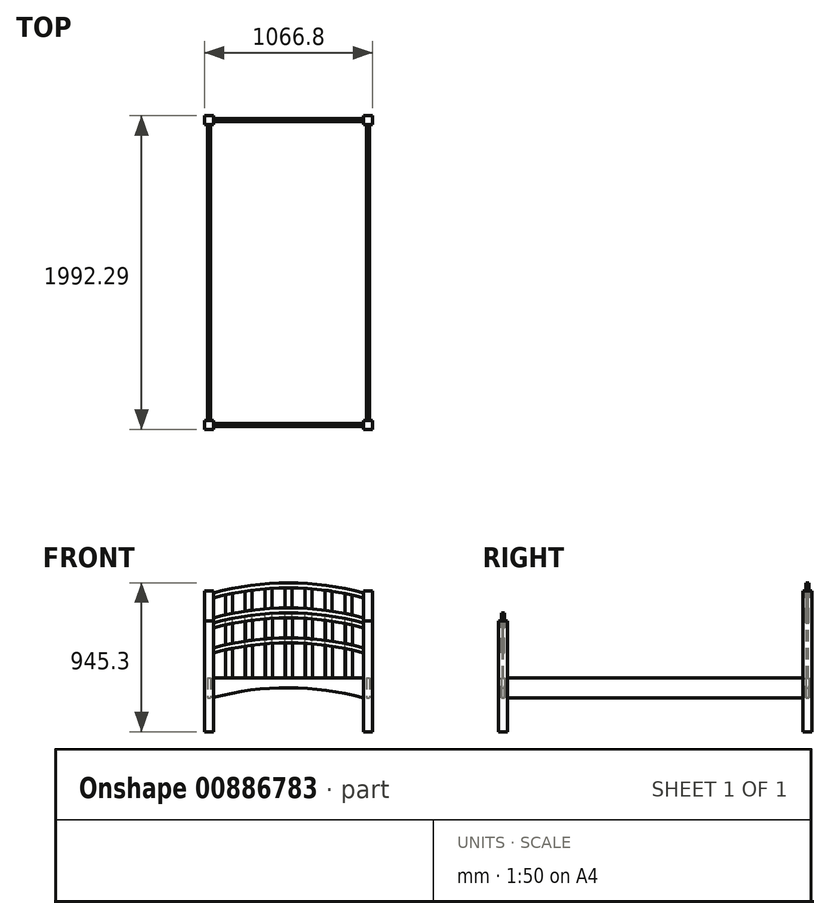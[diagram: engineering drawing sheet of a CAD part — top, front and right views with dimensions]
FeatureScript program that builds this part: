
annotation { "Feature Type Name" : "Feature", "Feature Type Description" : "" }
export const myFeature = defineFeature(function(context is Context, id is Id, definition is map)
    precondition{}
    {
        {
            var Q0;
            Q0=qCreatedBy(makeId("Front.planeOp"),FACE);
            var sketch = newSketch(context, id + "F0", { "sketchPlane" : qUnion([Q0])});
            skLineSegment(sketch, "E0.bottom", {"start": v(-533.4, 352.42) * mm, "end": v(-476.25, 352.42) * mm});
            skLineSegment(sketch, "E0.top", {"start": v(-533.4, -352.43) * mm, "end": v(-476.25, -352.43) * mm});
            skLineSegment(sketch, "E0.left", {"start": v(-533.4, 352.42) * mm, "end": v(-533.4, -352.43) * mm});
            skLineSegment(sketch, "E0.right", {"start": v(533.4, 352.43) * mm, "end": v(533.4, -352.42) * mm});
            skPoint(sketch, "E0.middle", {"position": v(0, 0) * mm});
            skLineSegment(sketch, "E1", {"start": v(-476.25, -352.43) * mm, "end": v(-476.25, 352.42) * mm});
            skLineSegment(sketch, "E2", {"start": v(476.25, 352.43) * mm, "end": v(476.25, -352.43) * mm});
            skPoint(sketch, "E3", {"position": v(0, -73.03) * mm});
            skLineSegment(sketch, "E4.trimOffspring", {"start": v(476.25, -352.43) * mm, "end": v(533.4, -352.42) * mm});
            skLineSegment(sketch, "E5.bottom", {"start": v(-476.25, -9.53) * mm, "end": v(476.25, -9.52) * mm});
            skArc(sketch, "E6", {"start": v(476.25, -136.53) * mm, "mid": v(0.11, -73.03) * mm, "end": v(-476.25, -134.82) * mm});
            skPoint(sketch, "E7", {"position": v(-476.25, 149.22) * mm});
            skPoint(sketch, "E8", {"position": v(-476.25, 180.97) * mm});
            skPoint(sketch, "E9", {"position": v(476.25, 180.97) * mm});
            skPoint(sketch, "E10", {"position": v(476.25, 149.22) * mm});
            skPoint(sketch, "E11", {"position": v(-476.25, 307.97) * mm});
            skPoint(sketch, "E12", {"position": v(-476.25, 339.72) * mm});
            skPoint(sketch, "E13", {"position": v(476.25, 339.73) * mm});
            skPoint(sketch, "E14", {"position": v(476.25, 307.98) * mm});
            skArc(sketch, "E15", {"start": v(476.25, 339.73) * mm, "mid": v(0, 402.37) * mm, "end": v(-476.25, 339.73) * mm});
            skArc(sketch, "E16", {"start": v(476.25, 307.97) * mm, "mid": v(0, 370.62) * mm, "end": v(-476.25, 307.97) * mm});
            skLineSegment(sketch, "E17.trimOffspring", {"start": v(476.25, 352.43) * mm, "end": v(533.4, 352.43) * mm});
            skArc(sketch, "E18", {"start": v(476.25, 180.98) * mm, "mid": v(0, 243.62) * mm, "end": v(-476.25, 180.98) * mm});
            skArc(sketch, "E19", {"start": v(476.25, 149.22) * mm, "mid": v(0, 211.87) * mm, "end": v(-476.25, 149.22) * mm});
            skLineSegment(sketch, "E20.bottom", {"start": v(-400.05, -9.53) * mm, "end": v(-355.6, -9.53) * mm});
            skLineSegment(sketch, "E20.left", {"start": v(-400.05, -9.53) * mm, "end": v(-400.05, 167.9) * mm});
            skLineSegment(sketch, "E20.right", {"start": v(-355.6, -9.53) * mm, "end": v(-355.6, 177.21) * mm});
            skLineSegment(sketch, "E21.1.0.0", {"start": v(-228.6, -9.53) * mm, "end": v(-228.6, 197.63) * mm});
            skLineSegment(sketch, "E21.1.0.1", {"start": v(-273.05, -9.53) * mm, "end": v(-273.05, 191.52) * mm});
            skLineSegment(sketch, "E21.1.0.2", {"start": v(-273.05, -9.53) * mm, "end": v(-228.6, -9.53) * mm});
            skLineSegment(sketch, "E21.2.0.0", {"start": v(-101.6, -9.53) * mm, "end": v(-101.6, 209.07) * mm});
            skLineSegment(sketch, "E21.2.0.1", {"start": v(-146.05, -9.53) * mm, "end": v(-146.05, 206.07) * mm});
            skLineSegment(sketch, "E21.2.0.2", {"start": v(-146.05, -9.53) * mm, "end": v(-101.6, -9.53) * mm});
            skLineSegment(sketch, "E21.3.0.0", {"start": v(25.4, -9.53) * mm, "end": v(25.4, 211.7) * mm});
            skLineSegment(sketch, "E21.3.0.1", {"start": v(-19.05, -9.53) * mm, "end": v(-19.05, 211.77) * mm});
            skLineSegment(sketch, "E21.3.0.2", {"start": v(-19.05, -9.53) * mm, "end": v(25.4, -9.53) * mm});
            skLineSegment(sketch, "E21.4.0.0", {"start": v(152.4, -9.53) * mm, "end": v(152.4, 205.56) * mm});
            skLineSegment(sketch, "E21.4.0.1", {"start": v(107.95, -9.53) * mm, "end": v(107.95, 208.7) * mm});
            skLineSegment(sketch, "E21.4.0.2", {"start": v(107.95, -9.53) * mm, "end": v(152.4, -9.53) * mm});
            skLineSegment(sketch, "E21.5.0.0", {"start": v(279.4, -9.53) * mm, "end": v(279.4, 190.55) * mm});
            skLineSegment(sketch, "E21.5.0.1", {"start": v(234.95, -9.53) * mm, "end": v(234.95, 196.82) * mm});
            skLineSegment(sketch, "E21.5.0.2", {"start": v(234.95, -9.53) * mm, "end": v(279.4, -9.53) * mm});
            skLineSegment(sketch, "E21.6.0.0", {"start": v(406.4, -9.53) * mm, "end": v(406.4, 166.47) * mm});
            skLineSegment(sketch, "E21.6.0.1", {"start": v(361.95, -9.53) * mm, "end": v(361.95, 175.95) * mm});
            skLineSegment(sketch, "E21.6.0.2", {"start": v(361.95, -9.53) * mm, "end": v(406.4, -9.53) * mm});
            skLineSegment(sketch, "E21.direction1", {"start": v(-355.6, -9.53) * mm, "end": v(-228.6, -9.53) * mm, "construction": true});
            skPoint(sketch, "E22.orphan", {"position": v(-400.05, 377.28) * mm});
            skPoint(sketch, "E23.orphan", {"position": v(-355.6, 377.28) * mm});
            skLineSegment(sketch, "E24.trimOffspring", {"start": v(-355.6, 208.96) * mm, "end": v(-355.6, 335.96) * mm});
            skLineSegment(sketch, "E25.trimOffspring", {"start": v(-400.05, 199.65) * mm, "end": v(-400.05, 326.65) * mm});
            skLineSegment(sketch, "E26.trimOffspring", {"start": v(-273.05, 223.27) * mm, "end": v(-273.05, 350.27) * mm});
            skLineSegment(sketch, "E27.trimOffspring", {"start": v(-228.6, 229.38) * mm, "end": v(-228.6, 356.38) * mm});
            skLineSegment(sketch, "E28.trimOffspring", {"start": v(-146.05, 237.82) * mm, "end": v(-146.05, 364.82) * mm});
            skLineSegment(sketch, "E29.trimOffspring", {"start": v(-101.6, 240.82) * mm, "end": v(-101.6, 367.82) * mm});
            skLineSegment(sketch, "E30.trimOffspring", {"start": v(-19.05, 243.52) * mm, "end": v(-19.05, 370.52) * mm});
            skLineSegment(sketch, "E31.trimOffspring", {"start": v(25.4, 243.45) * mm, "end": v(25.4, 370.45) * mm});
            skLineSegment(sketch, "E32.trimOffspring", {"start": v(107.95, 240.46) * mm, "end": v(107.95, 367.46) * mm});
            skLineSegment(sketch, "E33.trimOffspring", {"start": v(152.4, 237.3) * mm, "end": v(152.4, 364.3) * mm});
            skLineSegment(sketch, "E34.trimOffspring", {"start": v(234.95, 228.57) * mm, "end": v(234.95, 355.57) * mm});
            skLineSegment(sketch, "E35.trimOffspring", {"start": v(279.4, 222.3) * mm, "end": v(279.4, 349.3) * mm});
            skLineSegment(sketch, "E36.trimOffspring", {"start": v(361.95, 207.7) * mm, "end": v(361.95, 334.7) * mm});
            skLineSegment(sketch, "E37.trimOffspring", {"start": v(406.4, 198.22) * mm, "end": v(406.4, 325.22) * mm});
            skPoint(sketch, "E38.orphan", {"position": v(279.4, 377.28) * mm});
            skPoint(sketch, "E39.orphan", {"position": v(107.95, 377.28) * mm});
            skPoint(sketch, "E40.orphan", {"position": v(-19.05, 377.28) * mm});
            skPoint(sketch, "E41.orphan", {"position": v(-101.6, 377.28) * mm});
            skPoint(sketch, "E42.orphan", {"position": v(-228.6, 377.28) * mm});
            skSolve(sketch);
        }
        {
            var Q0;
            {var subQ3=sQuery(id+"F0.wireOp",EDGE,"E0.bottom");Q0=makeQuery(id+"F0.imprint","IMPRINT",FACE,{"disambiguationData":[TD([[makeQuery(id+"F0.imprint","IMPRINT",EDGE,{"derivedFrom":subQ3}),-1.0]])]});}
            var Q1;
            Q1=makeQuery(id+"F0.imprint","IMPRINT",FACE,{"disambiguationData":[TD([[makeQuery(id+"F0.imprint","IMPRINT",EDGE,{"derivedFrom":sQuery(id+"F0.wireOp",EDGE,"E0.right")}),-1.0]])]});
            extrude(context, id + "F1", {"entities" : qUnion([Q0, Q1]), "endBound" : BoundingType.SYMMETRIC, "depth" : 57.15 * mm, "offsetDistance" : 25.4 * mm});
        }
        {
            var Q0;
            {var subQ7=sQuery(id+"F0.wireOp",EDGE,"E15");Q0=makeQuery(id+"F0.imprint","IMPRINT",FACE,{"disambiguationData":[TD([[makeQuery(id+"F0.imprint","IMPRINT",EDGE,{"derivedFrom":subQ7}),1.0]])]});}
            var Q1;
            {var subQ8=sQuery(id+"F0.wireOp",EDGE,"E18");var subQ9=sQuery(id+"F0.wireOp",EDGE,"E1");var subQ10=makeQuery(id+"F0.imprint","INTERSECT",VERTEX,{"derivedFrom":[subQ9,subQ8]});Q1=makeQuery(id+"F0.imprint","IMPRINT",FACE,{"disambiguationData":[TD([[makeQuery(id+"F0.imprint","IMPRINT",EDGE,{"disambiguationData":[TD([[subQ10,1.0]])],"derivedFrom":subQ9}),-1.0]])]});}
            var Q2;
            {var subQ2=sQuery(id+"F0.wireOp",EDGE,"E5.left");Q2=makeQuery(id+"F0.imprint","IMPRINT",FACE,{"disambiguationData":[TD([[makeQuery(id+"F0.imprint","IMPRINT",EDGE,{"derivedFrom":subQ2}),1.0]])]});}
            var Q3;
            {var subQ13=sQuery(id+"F0.wireOp",EDGE,"E6");Q3=makeQuery(id+"F0.imprint","IMPRINT",FACE,{"disambiguationData":[TD([[makeQuery(id+"F0.imprint","IMPRINT",EDGE,{"derivedFrom":subQ13}),-1.0]])]});}
            extrude(context, id + "F2", {"entities" : qUnion([Q0, Q1, Q2, Q3]), "endBound" : BoundingType.SYMMETRIC, "depth" : 19.05 * mm, "offsetDistance" : 25.4 * mm});
        }
        {
            var Q0;
            {var subQ2=sQuery(id+"F0.wireOp",EDGE,"E20.left");Q0=makeQuery(id+"F0.imprint","IMPRINT",FACE,{"disambiguationData":[TD([[makeQuery(id+"F0.imprint","IMPRINT",EDGE,{"derivedFrom":subQ2}),-1.0]])]});}
            var Q1;
            {var subQ0=sQuery(id+"F0.wireOp",EDGE,"E21.1.0.0");Q1=makeQuery(id+"F0.imprint","IMPRINT",FACE,{"disambiguationData":[TD([[makeQuery(id+"F0.imprint","IMPRINT",EDGE,{"derivedFrom":subQ0}),1.0]])]});}
            var Q2;
            {var subQ0=sQuery(id+"F0.wireOp",EDGE,"E24.trimOffspring");Q2=makeQuery(id+"F0.imprint","IMPRINT",FACE,{"disambiguationData":[TD([[makeQuery(id+"F0.imprint","IMPRINT",EDGE,{"derivedFrom":subQ0}),1.0]])]});}
            var Q3;
            {var subQ0=sQuery(id+"F0.wireOp",EDGE,"E26.trimOffspring");Q3=makeQuery(id+"F0.imprint","IMPRINT",FACE,{"disambiguationData":[TD([[makeQuery(id+"F0.imprint","IMPRINT",EDGE,{"derivedFrom":subQ0}),-1.0]])]});}
            var Q4;
            {var subQ0=sQuery(id+"F0.wireOp",EDGE,"E28.trimOffspring");Q4=makeQuery(id+"F0.imprint","IMPRINT",FACE,{"disambiguationData":[TD([[makeQuery(id+"F0.imprint","IMPRINT",EDGE,{"derivedFrom":subQ0}),-1.0]])]});}
            var Q5;
            {var subQ0=sQuery(id+"F0.wireOp",EDGE,"E21.2.0.0");Q5=makeQuery(id+"F0.imprint","IMPRINT",FACE,{"disambiguationData":[TD([[makeQuery(id+"F0.imprint","IMPRINT",EDGE,{"derivedFrom":subQ0}),1.0]])]});}
            var Q6;
            {var subQ0=sQuery(id+"F0.wireOp",EDGE,"E21.3.0.0");Q6=makeQuery(id+"F0.imprint","IMPRINT",FACE,{"disambiguationData":[TD([[makeQuery(id+"F0.imprint","IMPRINT",EDGE,{"derivedFrom":subQ0}),1.0]])]});}
            var Q7;
            {var subQ0=sQuery(id+"F0.wireOp",EDGE,"E30.trimOffspring");Q7=makeQuery(id+"F0.imprint","IMPRINT",FACE,{"disambiguationData":[TD([[makeQuery(id+"F0.imprint","IMPRINT",EDGE,{"derivedFrom":subQ0}),-1.0]])]});}
            var Q8;
            {var subQ0=sQuery(id+"F0.wireOp",EDGE,"E32.trimOffspring");Q8=makeQuery(id+"F0.imprint","IMPRINT",FACE,{"disambiguationData":[TD([[makeQuery(id+"F0.imprint","IMPRINT",EDGE,{"derivedFrom":subQ0}),-1.0]])]});}
            var Q9;
            {var subQ0=sQuery(id+"F0.wireOp",EDGE,"E21.4.0.0");Q9=makeQuery(id+"F0.imprint","IMPRINT",FACE,{"disambiguationData":[TD([[makeQuery(id+"F0.imprint","IMPRINT",EDGE,{"derivedFrom":subQ0}),1.0]])]});}
            var Q10;
            {var subQ0=sQuery(id+"F0.wireOp",EDGE,"E21.5.0.0");Q10=makeQuery(id+"F0.imprint","IMPRINT",FACE,{"disambiguationData":[TD([[makeQuery(id+"F0.imprint","IMPRINT",EDGE,{"derivedFrom":subQ0}),1.0]])]});}
            var Q11;
            {var subQ0=sQuery(id+"F0.wireOp",EDGE,"E34.trimOffspring");Q11=makeQuery(id+"F0.imprint","IMPRINT",FACE,{"disambiguationData":[TD([[makeQuery(id+"F0.imprint","IMPRINT",EDGE,{"derivedFrom":subQ0}),-1.0]])]});}
            var Q12;
            {var subQ0=sQuery(id+"F0.wireOp",EDGE,"E36.trimOffspring");Q12=makeQuery(id+"F0.imprint","IMPRINT",FACE,{"disambiguationData":[TD([[makeQuery(id+"F0.imprint","IMPRINT",EDGE,{"derivedFrom":subQ0}),-1.0]])]});}
            var Q13;
            {var subQ0=sQuery(id+"F0.wireOp",EDGE,"E21.6.0.0");Q13=makeQuery(id+"F0.imprint","IMPRINT",FACE,{"disambiguationData":[TD([[makeQuery(id+"F0.imprint","IMPRINT",EDGE,{"derivedFrom":subQ0}),1.0]])]});}
            extrude(context, id + "F3", {"entities" : qUnion([Q0, Q1, Q2, Q3, Q4, Q5, Q6, Q7, Q8, Q9, Q10, Q11, Q12, Q13]), "endBound" : BoundingType.SYMMETRIC, "depth" : 6.35 * mm, "offsetDistance" : 25.4 * mm});
        }
        {
            var Q0;
            Q0=qCreatedBy(makeId("Front.planeOp"),FACE);
            cPlane(context, id + "F4", {"entities" : qUnion([Q0]), "cplaneType" : CPlaneType.OFFSET, "offset" : 1935.15 * mm, "oppositeDirection" : true, "width" : 152.4 * mm, "height" : 152.4 * mm});
        }
        {
            var Q0;
            Q0=qCreatedBy(id+"F4.planeOp",FACE);
            var sketch = newSketch(context, id + "F5", { "sketchPlane" : qUnion([Q0])});
            skLineSegment(sketch, "E43.bottom", {"start": v(-533.4, 542.93) * mm, "end": v(-476.25, 542.93) * mm});
            skLineSegment(sketch, "E43.top", {"start": v(-533.4, -352.42) * mm, "end": v(-476.25, -352.42) * mm});
            skLineSegment(sketch, "E43.left", {"start": v(-533.4, 542.93) * mm, "end": v(-533.4, -352.42) * mm});
            skLineSegment(sketch, "E43.right", {"start": v(533.4, 542.92) * mm, "end": v(533.4, -352.42) * mm});
            skPoint(sketch, "E43.middle", {"position": v(0, 95.25) * mm});
            skLineSegment(sketch, "E44", {"start": v(-476.25, -352.42) * mm, "end": v(-476.25, 542.93) * mm});
            skLineSegment(sketch, "E45", {"start": v(476.25, 542.93) * mm, "end": v(476.25, -352.42) * mm});
            skPoint(sketch, "E46", {"position": v(0, -73.02) * mm});
            skLineSegment(sketch, "E47.trimOffspring", {"start": v(476.25, -352.42) * mm, "end": v(533.4, -352.42) * mm});
            skLineSegment(sketch, "E48.bottom", {"start": v(-476.25, -9.52) * mm, "end": v(482.61, -9.52) * mm});
            skArc(sketch, "E49", {"start": v(476.25, -136.52) * mm, "mid": v(-3.18, -73.02) * mm, "end": v(-482.61, -136.52) * mm});
            skPoint(sketch, "E50", {"position": v(-476.25, 339.73) * mm});
            skPoint(sketch, "E51", {"position": v(-476.25, 371.48) * mm});
            skPoint(sketch, "E52", {"position": v(476.25, 371.48) * mm});
            skPoint(sketch, "E53", {"position": v(476.25, 339.73) * mm});
            skPoint(sketch, "E54", {"position": v(-476.25, 498.48) * mm});
            skPoint(sketch, "E55", {"position": v(-476.25, 530.23) * mm});
            skPoint(sketch, "E56", {"position": v(476.25, 530.23) * mm});
            skPoint(sketch, "E57", {"position": v(476.25, 498.48) * mm});
            skArc(sketch, "E58", {"start": v(476.25, 530.23) * mm, "mid": v(0, 592.87) * mm, "end": v(-476.25, 530.23) * mm});
            skArc(sketch, "E59", {"start": v(476.25, 498.48) * mm, "mid": v(0, 561.12) * mm, "end": v(-476.25, 498.48) * mm});
            skLineSegment(sketch, "E60.trimOffspring", {"start": v(476.25, 542.92) * mm, "end": v(533.4, 542.93) * mm});
            skArc(sketch, "E61", {"start": v(476.25, 371.48) * mm, "mid": v(0, 434.12) * mm, "end": v(-476.25, 371.48) * mm});
            skArc(sketch, "E62", {"start": v(476.25, 339.73) * mm, "mid": v(0, 402.37) * mm, "end": v(-476.25, 339.73) * mm});
            skLineSegment(sketch, "E63.bottom", {"start": v(-400.05, -9.52) * mm, "end": v(-355.6, -55.36) * mm});
            skLineSegment(sketch, "E63.left", {"start": v(-400.05, -9.52) * mm, "end": v(-400.05, 358.4) * mm});
            skLineSegment(sketch, "E63.right", {"start": v(-355.6, -55.36) * mm, "end": v(-355.6, 367.71) * mm});
            skLineSegment(sketch, "E64.1.0.0", {"start": v(-228.6, -55.36) * mm, "end": v(-231.36, 387.78) * mm});
            skLineSegment(sketch, "E64.1.0.1", {"start": v(-274.45, -55.36) * mm, "end": v(-275.75, 381.6) * mm});
            skLineSegment(sketch, "E64.1.0.2", {"start": v(-274.45, -55.36) * mm, "end": v(-228.6, -55.36) * mm});
            skLineSegment(sketch, "E64.2.0.0", {"start": v(-104.77, -25.27) * mm, "end": v(-104.78, 399.39) * mm});
            skLineSegment(sketch, "E64.2.0.1", {"start": v(-149.23, -25.27) * mm, "end": v(-149.23, 396.32) * mm});
            skLineSegment(sketch, "E64.2.0.2", {"start": v(-149.23, -25.27) * mm, "end": v(-104.77, -25.27) * mm});
            skLineSegment(sketch, "E64.3.0.0", {"start": v(22.23, -23.95) * mm, "end": v(22.22, 402.24) * mm});
            skLineSegment(sketch, "E64.3.0.1", {"start": v(-22.22, -23.95) * mm, "end": v(-22.23, 402.24) * mm});
            skLineSegment(sketch, "E64.3.0.2", {"start": v(-22.22, -23.95) * mm, "end": v(22.23, -23.95) * mm});
            skLineSegment(sketch, "E64.4.0.0", {"start": v(149.23, -20) * mm, "end": v(149.22, 396.32) * mm});
            skLineSegment(sketch, "E64.4.0.1", {"start": v(104.78, -20) * mm, "end": v(104.77, 399.39) * mm});
            skLineSegment(sketch, "E64.4.0.2", {"start": v(104.78, -20) * mm, "end": v(149.23, -20) * mm});
            skLineSegment(sketch, "E64.5.0.0", {"start": v(276.23, -22.64) * mm, "end": v(276.22, 381.54) * mm});
            skLineSegment(sketch, "E64.5.0.1", {"start": v(231.77, -22.64) * mm, "end": v(231.77, 387.73) * mm});
            skLineSegment(sketch, "E64.5.0.2", {"start": v(231.77, -22.64) * mm, "end": v(276.23, -22.64) * mm});
            skLineSegment(sketch, "E64.6.0.0", {"start": v(403.23, -25.27) * mm, "end": v(403.22, 357.69) * mm});
            skLineSegment(sketch, "E64.6.0.1", {"start": v(358.78, -25.27) * mm, "end": v(358.77, 367.09) * mm});
            skLineSegment(sketch, "E64.6.0.2", {"start": v(358.78, -25.27) * mm, "end": v(403.23, -25.27) * mm});
            skLineSegment(sketch, "E64.direction1", {"start": v(-355.6, -55.36) * mm, "end": v(-228.6, -55.36) * mm, "construction": true});
            skPoint(sketch, "E65.orphan", {"position": v(-400.05, 567.78) * mm});
            skPoint(sketch, "E66.orphan", {"position": v(-355.6, 567.78) * mm});
            skLineSegment(sketch, "E67.trimOffspring", {"start": v(-355.6, 399.46) * mm, "end": v(-355.6, 526.46) * mm});
            skLineSegment(sketch, "E68.trimOffspring", {"start": v(-400.05, 390.15) * mm, "end": v(-400.05, 517.15) * mm});
            skLineSegment(sketch, "E69.trimOffspring", {"start": v(-275.85, 413.35) * mm, "end": v(-276.23, 540.29) * mm});
            skLineSegment(sketch, "E70.trimOffspring", {"start": v(-231.55, 419.5) * mm, "end": v(-232.34, 546.4) * mm});
            skLineSegment(sketch, "E71.trimOffspring", {"start": v(-149.23, 428.07) * mm, "end": v(-149.23, 555.07) * mm});
            skLineSegment(sketch, "E72.trimOffspring", {"start": v(-104.78, 431.14) * mm, "end": v(-104.78, 558.14) * mm});
            skLineSegment(sketch, "E73.trimOffspring", {"start": v(-22.23, 433.99) * mm, "end": v(-22.23, 560.99) * mm});
            skLineSegment(sketch, "E74.trimOffspring", {"start": v(22.22, 433.99) * mm, "end": v(22.22, 560.99) * mm});
            skLineSegment(sketch, "E75.trimOffspring", {"start": v(104.77, 431.14) * mm, "end": v(104.77, 558.14) * mm});
            skLineSegment(sketch, "E76.trimOffspring", {"start": v(149.22, 428.07) * mm, "end": v(149.22, 555.07) * mm});
            skLineSegment(sketch, "E77.trimOffspring", {"start": v(231.77, 419.48) * mm, "end": v(231.77, 546.48) * mm});
            skLineSegment(sketch, "E78.trimOffspring", {"start": v(276.22, 413.29) * mm, "end": v(276.22, 540.29) * mm});
            skLineSegment(sketch, "E79.trimOffspring", {"start": v(358.77, 398.84) * mm, "end": v(358.77, 525.84) * mm});
            skLineSegment(sketch, "E80.trimOffspring", {"start": v(403.22, 389.44) * mm, "end": v(403.22, 516.44) * mm});
            skPoint(sketch, "E81.orphan", {"position": v(276.22, 566.92) * mm});
            skPoint(sketch, "E82.orphan", {"position": v(104.77, 566.92) * mm});
            skPoint(sketch, "E83.orphan", {"position": v(-22.23, 566.92) * mm});
            skPoint(sketch, "E84.orphan", {"position": v(-104.78, 566.92) * mm});
            skPoint(sketch, "E85.orphan", {"position": v(-232.47, 567.13) * mm});
            skSolve(sketch);
        }
        {
            var Q0;
            {var subQ3=sQuery(id+"F5.wireOp",EDGE,"E43.bottom");Q0=makeQuery(id+"F5.imprint","IMPRINT",FACE,{"disambiguationData":[TD([[makeQuery(id+"F5.imprint","IMPRINT",EDGE,{"derivedFrom":subQ3}),-1.0]])]});}
            var Q1;
            Q1=makeQuery(id+"F5.imprint","IMPRINT",FACE,{"disambiguationData":[TD([[makeQuery(id+"F5.imprint","IMPRINT",EDGE,{"derivedFrom":sQuery(id+"F5.wireOp",EDGE,"E43.right")}),-1.0]])]});
            extrude(context, id + "F6", {"entities" : qUnion([Q0, Q1]), "endBound" : BoundingType.SYMMETRIC, "depth" : 57.15 * mm, "offsetDistance" : 25.4 * mm});
        }
        {
            var Q0;
            {var subQ8=sQuery(id+"F5.wireOp",EDGE,"E61");var subQ9=sQuery(id+"F5.wireOp",EDGE,"E44");var subQ10=makeQuery(id+"F5.imprint","INTERSECT",VERTEX,{"derivedFrom":[subQ9,subQ8]});Q0=makeQuery(id+"F5.imprint","IMPRINT",FACE,{"disambiguationData":[TD([[makeQuery(id+"F5.imprint","IMPRINT",EDGE,{"disambiguationData":[TD([[subQ10,1.0]])],"derivedFrom":subQ9}),-1.0]])]});}
            var Q1;
            {var subQ15=sQuery(id+"F5.wireOp",EDGE,"E48.left");Q1=makeQuery(id+"F5.imprint","IMPRINT",FACE,{"disambiguationData":[TD([[makeQuery(id+"F5.imprint","IMPRINT",EDGE,{"derivedFrom":subQ15}),1.0]])]});}
            var Q2;
            {var subQ8=sQuery(id+"F5.wireOp",EDGE,"E58");Q2=makeQuery(id+"F5.imprint","IMPRINT",FACE,{"disambiguationData":[TD([[makeQuery(id+"F5.imprint","IMPRINT",EDGE,{"derivedFrom":subQ8}),1.0]])]});}
            var Q3;
            {var subQ5=sQuery(id+"F5.wireOp",EDGE,"E64.1.0.2");Q3=makeQuery(id+"F5.imprint","IMPRINT",FACE,{"disambiguationData":[TD([[makeQuery(id+"F5.imprint","IMPRINT",EDGE,{"derivedFrom":subQ5}),1.0]])]});}
            var Q4;
            {var subQ0=sQuery(id+"F5.wireOp",EDGE,"E63.bottom");Q4=makeQuery(id+"F5.imprint","IMPRINT",FACE,{"disambiguationData":[TD([[makeQuery(id+"F5.imprint","IMPRINT",EDGE,{"derivedFrom":subQ0}),1.0]])]});}
            var Q5;
            {var subQ5=sQuery(id+"F5.wireOp",EDGE,"E64.2.0.2");Q5=makeQuery(id+"F5.imprint","IMPRINT",FACE,{"disambiguationData":[TD([[makeQuery(id+"F5.imprint","IMPRINT",EDGE,{"derivedFrom":subQ5}),1.0]])]});}
            var Q6;
            {var subQ5=sQuery(id+"F5.wireOp",EDGE,"E64.3.0.2");Q6=makeQuery(id+"F5.imprint","IMPRINT",FACE,{"disambiguationData":[TD([[makeQuery(id+"F5.imprint","IMPRINT",EDGE,{"derivedFrom":subQ5}),1.0]])]});}
            var Q7;
            {var subQ5=sQuery(id+"F5.wireOp",EDGE,"E64.4.0.2");Q7=makeQuery(id+"F5.imprint","IMPRINT",FACE,{"disambiguationData":[TD([[makeQuery(id+"F5.imprint","IMPRINT",EDGE,{"derivedFrom":subQ5}),1.0]])]});}
            var Q8;
            {var subQ5=sQuery(id+"F5.wireOp",EDGE,"E64.5.0.2");Q8=makeQuery(id+"F5.imprint","IMPRINT",FACE,{"disambiguationData":[TD([[makeQuery(id+"F5.imprint","IMPRINT",EDGE,{"derivedFrom":subQ5}),1.0]])]});}
            var Q9;
            {var subQ5=sQuery(id+"F5.wireOp",EDGE,"E64.6.0.2");Q9=makeQuery(id+"F5.imprint","IMPRINT",FACE,{"disambiguationData":[TD([[makeQuery(id+"F5.imprint","IMPRINT",EDGE,{"derivedFrom":subQ5}),1.0]])]});}
            var Q10;
            {var subQ10=sQuery(id+"F5.wireOp",EDGE,"E63.bottom");Q10=makeQuery(id+"F5.imprint","IMPRINT",FACE,{"disambiguationData":[TD([[makeQuery(id+"F5.imprint","IMPRINT",EDGE,{"derivedFrom":subQ10}),-1.0]])]});}
            extrude(context, id + "F7", {"entities" : qUnion([Q0, Q1, Q2, Q3, Q4, Q5, Q6, Q7, Q8, Q9, Q10]), "endBound" : BoundingType.SYMMETRIC, "depth" : 19.05 * mm, "offsetDistance" : 25.4 * mm});
        }
        {
            var Q0;
            {var subQ0=sQuery(id+"F5.wireOp",EDGE,"E63.left");Q0=makeQuery(id+"F5.imprint","IMPRINT",FACE,{"disambiguationData":[TD([[makeQuery(id+"F5.imprint","IMPRINT",EDGE,{"derivedFrom":subQ0}),-1.0]])]});}
            var Q1;
            {var subQ0=sQuery(id+"F5.wireOp",EDGE,"E67.trimOffspring");Q1=makeQuery(id+"F5.imprint","IMPRINT",FACE,{"disambiguationData":[TD([[makeQuery(id+"F5.imprint","IMPRINT",EDGE,{"derivedFrom":subQ0}),1.0]])]});}
            var Q2;
            {var subQ0=sQuery(id+"F5.wireOp",EDGE,"E69.trimOffspring");Q2=makeQuery(id+"F5.imprint","IMPRINT",FACE,{"disambiguationData":[TD([[makeQuery(id+"F5.imprint","IMPRINT",EDGE,{"derivedFrom":subQ0}),-1.0]])]});}
            var Q3;
            {var subQ0=sQuery(id+"F5.wireOp",EDGE,"E64.1.0.1");var subQ1=sQuery(id+"F5.wireOp",EDGE,"E48.bottom");var subQ2=makeQuery(id+"F5.imprint","INTERSECT",VERTEX,{"derivedFrom":[subQ1,subQ0]});Q3=makeQuery(id+"F5.imprint","IMPRINT",FACE,{"disambiguationData":[TD([[makeQuery(id+"F5.imprint","IMPRINT",EDGE,{"disambiguationData":[TD([[subQ2,-1.0]])],"derivedFrom":subQ1}),1.0]])]});}
            var Q4;
            {var subQ0=sQuery(id+"F5.wireOp",EDGE,"E64.2.0.1");var subQ1=sQuery(id+"F5.wireOp",EDGE,"E48.bottom");var subQ2=makeQuery(id+"F5.imprint","INTERSECT",VERTEX,{"derivedFrom":[subQ1,subQ0]});Q4=makeQuery(id+"F5.imprint","IMPRINT",FACE,{"disambiguationData":[TD([[makeQuery(id+"F5.imprint","IMPRINT",EDGE,{"disambiguationData":[TD([[subQ2,-1.0]])],"derivedFrom":subQ1}),1.0]])]});}
            var Q5;
            {var subQ0=sQuery(id+"F5.wireOp",EDGE,"E71.trimOffspring");Q5=makeQuery(id+"F5.imprint","IMPRINT",FACE,{"disambiguationData":[TD([[makeQuery(id+"F5.imprint","IMPRINT",EDGE,{"derivedFrom":subQ0}),-1.0]])]});}
            var Q6;
            {var subQ0=sQuery(id+"F5.wireOp",EDGE,"E73.trimOffspring");Q6=makeQuery(id+"F5.imprint","IMPRINT",FACE,{"disambiguationData":[TD([[makeQuery(id+"F5.imprint","IMPRINT",EDGE,{"derivedFrom":subQ0}),-1.0]])]});}
            var Q7;
            {var subQ0=sQuery(id+"F5.wireOp",EDGE,"E64.3.0.1");var subQ1=sQuery(id+"F5.wireOp",EDGE,"E48.bottom");var subQ2=makeQuery(id+"F5.imprint","INTERSECT",VERTEX,{"derivedFrom":[subQ1,subQ0]});Q7=makeQuery(id+"F5.imprint","IMPRINT",FACE,{"disambiguationData":[TD([[makeQuery(id+"F5.imprint","IMPRINT",EDGE,{"disambiguationData":[TD([[subQ2,-1.0]])],"derivedFrom":subQ1}),1.0]])]});}
            var Q8;
            {var subQ0=sQuery(id+"F5.wireOp",EDGE,"E64.4.0.1");var subQ1=sQuery(id+"F5.wireOp",EDGE,"E48.bottom");var subQ2=makeQuery(id+"F5.imprint","INTERSECT",VERTEX,{"derivedFrom":[subQ1,subQ0]});Q8=makeQuery(id+"F5.imprint","IMPRINT",FACE,{"disambiguationData":[TD([[makeQuery(id+"F5.imprint","IMPRINT",EDGE,{"disambiguationData":[TD([[subQ2,-1.0]])],"derivedFrom":subQ1}),1.0]])]});}
            var Q9;
            {var subQ0=sQuery(id+"F5.wireOp",EDGE,"E75.trimOffspring");Q9=makeQuery(id+"F5.imprint","IMPRINT",FACE,{"disambiguationData":[TD([[makeQuery(id+"F5.imprint","IMPRINT",EDGE,{"derivedFrom":subQ0}),-1.0]])]});}
            var Q10;
            {var subQ0=sQuery(id+"F5.wireOp",EDGE,"E64.5.0.1");var subQ1=sQuery(id+"F5.wireOp",EDGE,"E48.bottom");var subQ2=makeQuery(id+"F5.imprint","INTERSECT",VERTEX,{"derivedFrom":[subQ1,subQ0]});Q10=makeQuery(id+"F5.imprint","IMPRINT",FACE,{"disambiguationData":[TD([[makeQuery(id+"F5.imprint","IMPRINT",EDGE,{"disambiguationData":[TD([[subQ2,-1.0]])],"derivedFrom":subQ1}),1.0]])]});}
            var Q11;
            {var subQ0=sQuery(id+"F5.wireOp",EDGE,"E77.trimOffspring");Q11=makeQuery(id+"F5.imprint","IMPRINT",FACE,{"disambiguationData":[TD([[makeQuery(id+"F5.imprint","IMPRINT",EDGE,{"derivedFrom":subQ0}),-1.0]])]});}
            var Q12;
            {var subQ0=sQuery(id+"F5.wireOp",EDGE,"E79.trimOffspring");Q12=makeQuery(id+"F5.imprint","IMPRINT",FACE,{"disambiguationData":[TD([[makeQuery(id+"F5.imprint","IMPRINT",EDGE,{"derivedFrom":subQ0}),-1.0]])]});}
            var Q13;
            {var subQ0=sQuery(id+"F5.wireOp",EDGE,"E64.6.0.1");var subQ1=sQuery(id+"F5.wireOp",EDGE,"E48.bottom");var subQ2=makeQuery(id+"F5.imprint","INTERSECT",VERTEX,{"derivedFrom":[subQ1,subQ0]});Q13=makeQuery(id+"F5.imprint","IMPRINT",FACE,{"disambiguationData":[TD([[makeQuery(id+"F5.imprint","IMPRINT",EDGE,{"disambiguationData":[TD([[subQ2,-1.0]])],"derivedFrom":subQ1}),1.0]])]});}
            extrude(context, id + "F8", {"entities" : qUnion([Q0, Q1, Q2, Q3, Q4, Q5, Q6, Q7, Q8, Q9, Q10, Q11, Q12, Q13]), "endBound" : BoundingType.SYMMETRIC, "depth" : 12.7 * mm, "offsetDistance" : 25.4 * mm});
        }
        {
            var Q0;
            Q0=makeQuery(id+"F6.opExtrude","CAP_FACE",FACE,{"disambiguationData":[OSD([sQuery(id+"F5.wireOp",EDGE,"E43.right"),sQuery(id+"F5.wireOp",EDGE,"E45"),sQuery(id+"F5.wireOp",EDGE,"E47.trimOffspring"),sQuery(id+"F5.wireOp",EDGE,"E48.right"),sQuery(id+"F5.wireOp",EDGE,"E60.trimOffspring")])],"isStart":false});
            var sketch = newSketch(context, id + "F9", { "sketchPlane" : qUnion([Q0])});
            skLineSegment(sketch, "E86.bottom", {"start": v(495.3, -9.52) * mm, "end": v(514.35, -9.52) * mm});
            skLineSegment(sketch, "E86.top", {"start": v(495.3, -136.52) * mm, "end": v(514.35, -136.52) * mm});
            skLineSegment(sketch, "E86.left", {"start": v(495.3, -9.52) * mm, "end": v(495.3, -136.52) * mm});
            skLineSegment(sketch, "E86.right", {"start": v(514.35, -9.52) * mm, "end": v(514.35, -136.52) * mm});
            skSolve(sketch);
        }
        {
            var Q0;
            Q0=makeQuery(id+"F6.opExtrude","CAP_FACE",FACE,{"disambiguationData":[OSD([sQuery(id+"F5.wireOp",EDGE,"E43.bottom"),sQuery(id+"F5.wireOp",EDGE,"E43.top"),sQuery(id+"F5.wireOp",EDGE,"E43.left"),sQuery(id+"F5.wireOp",EDGE,"E44"),sQuery(id+"F5.wireOp",EDGE,"E48.left")])],"isStart":false});
            var sketch = newSketch(context, id + "F10", { "sketchPlane" : qUnion([Q0])});
            skLineSegment(sketch, "E87.bottom", {"start": v(-514.35, -9.53) * mm, "end": v(-495.3, -9.53) * mm});
            skLineSegment(sketch, "E87.top", {"start": v(-514.35, -136.53) * mm, "end": v(-495.3, -136.53) * mm});
            skLineSegment(sketch, "E87.left", {"start": v(-514.35, -9.53) * mm, "end": v(-514.35, -136.53) * mm});
            skLineSegment(sketch, "E87.right", {"start": v(-495.3, -9.53) * mm, "end": v(-495.3, -136.53) * mm});
            skSolve(sketch);
        }
        {
            var Q0;
            Q0 = qSketchRegion(id + "F9", true);
            var Q1;
            Q1=makeQuery(id+"F10.imprint","IMPRINT",FACE,{"disambiguationData":[TD([[makeQuery(id+"F10.imprint","IMPRINT",EDGE,{"derivedFrom":sQuery(id+"F10.wireOp",EDGE,"E87.bottom")}),-1.0]])]});
            extrude(context, id + "F11", {"entities" : qUnion([Q0, Q1]), "depth" : 1879.6 * mm, "offsetDistance" : 25.4 * mm});
        }
    });
